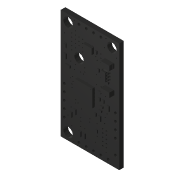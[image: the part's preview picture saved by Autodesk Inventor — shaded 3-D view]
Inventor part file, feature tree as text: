
AUTODESK INVENTOR PART (.ipt)
format: ipt  version: 2018 (Build 220112000, 112)  size: 213,504 bytes
history: native  units: in
note: dims shown in document units (in); Inventor stores cm internally (conversion verified against a paired STEP export)
features: sketch x1, other x1
ambient origin geometry x8: Origin, YZ Plane, XZ Plane, XY Plane, X Axis, Y Axis, Z Axis, Center Point
feature tree (2):
  sketch  "Sketch1"  dims[d0=0.601in d1=1.3in d2=0.15in d3=0.35in d4=0.45in d5=0.35in]
  other  "MeshFeature1"
